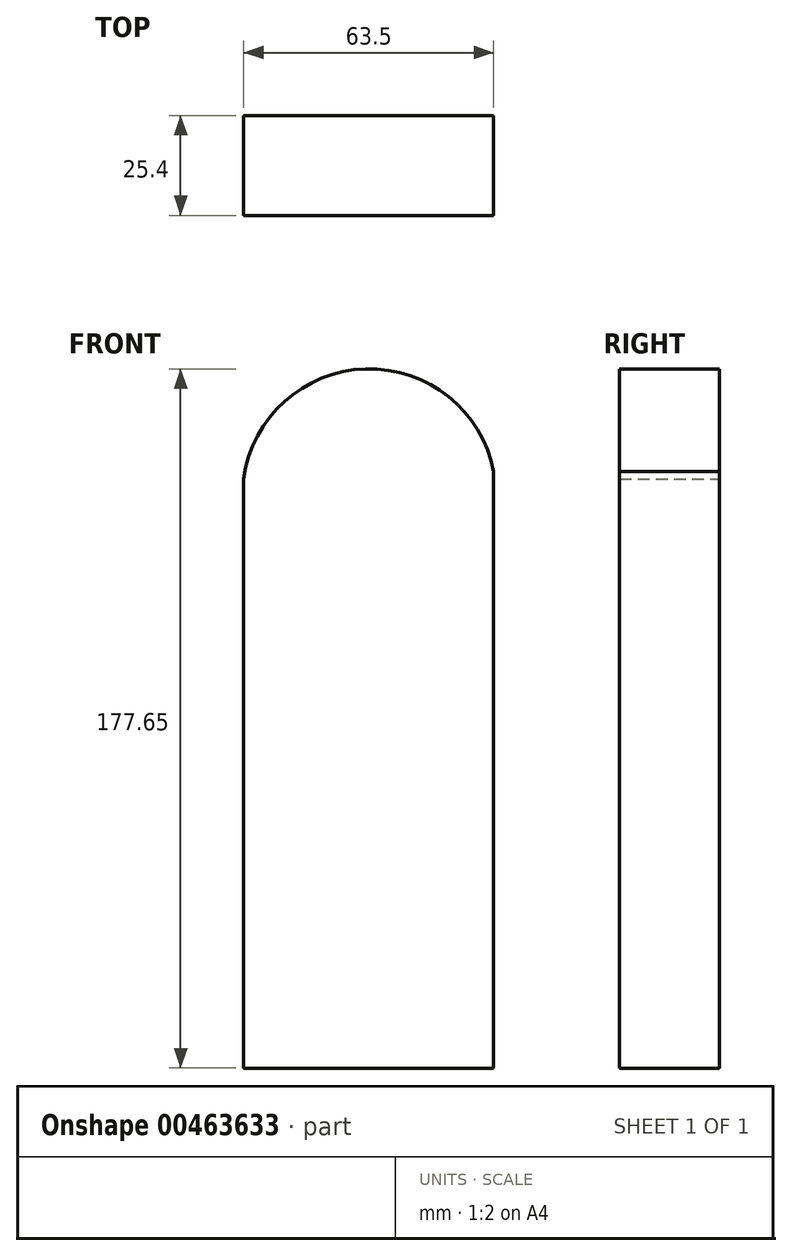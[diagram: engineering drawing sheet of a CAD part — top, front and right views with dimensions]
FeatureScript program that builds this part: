
annotation { "Feature Type Name" : "Feature", "Feature Type Description" : "" }
export const myFeature = defineFeature(function(context is Context, id is Id, definition is map)
    precondition{}
    {
        {
            var Q0;
            Q0=qCreatedBy(makeId("Front.planeOp"),FACE);
            var sketch = newSketch(context, id + "F0", { "sketchPlane" : qUnion([Q0])});
            skLineSegment(sketch, "E0.top", {"start": v(-100.4, -82.11) * mm, "end": v(-36.9, -82.11) * mm});
            skLineSegment(sketch, "E0.left", {"start": v(-100.4, 67.55) * mm, "end": v(-100.4, -82.11) * mm});
            skLineSegment(sketch, "E0.right", {"start": v(-36.9, 69.41) * mm, "end": v(-36.9, -82.11) * mm});
            skArc(sketch, "E1", {"start": v(-36.9, 69.41) * mm, "mid": v(-69.44, 95.53) * mm, "end": v(-100.4, 67.55) * mm});
            skSolve(sketch);
        }
        {
            var Q0;
            Q0=makeQuery(id+"F0.imprint","IMPRINT",FACE,{"disambiguationData":[TD([[makeQuery(id+"F0.imprint","IMPRINT",EDGE,{"derivedFrom":sQuery(id+"F0.wireOp",EDGE,"E0.top")}),1.0]])]});
            extrude(context, id + "F1", {"entities" : qUnion([Q0]), "depth" : 25.4 * mm});
        }
    });
